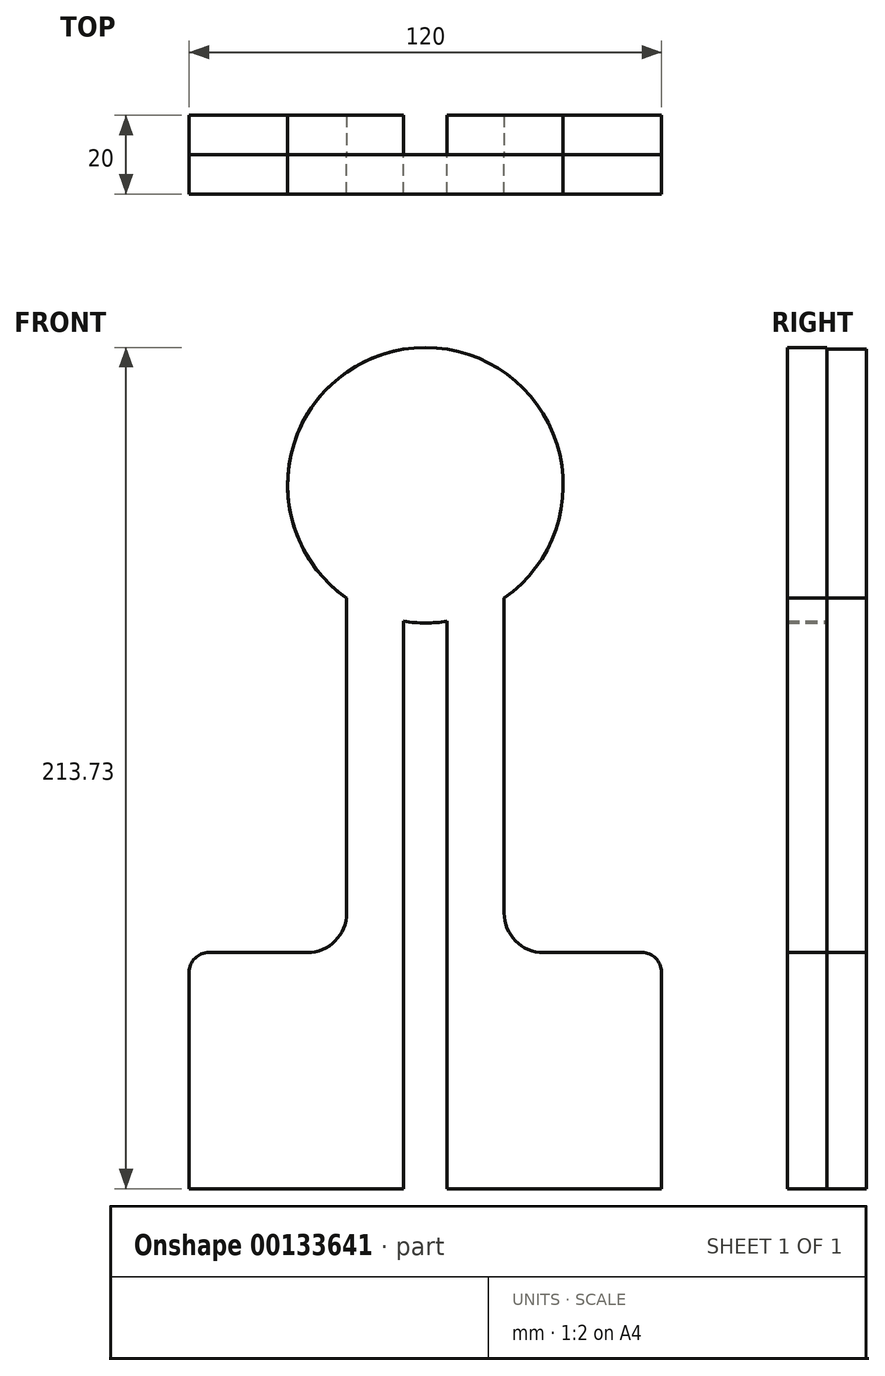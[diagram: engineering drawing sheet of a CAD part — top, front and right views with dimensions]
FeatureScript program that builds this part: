
annotation { "Feature Type Name" : "Feature", "Feature Type Description" : "" }
export const myFeature = defineFeature(function(context is Context, id is Id, definition is map)
    precondition{}
    {
        {
            var Q0;
            Q0=qCreatedBy(makeId("Front.planeOp"),FACE);
            var sketch = newSketch(context, id + "F0", { "sketchPlane" : qUnion([Q0])});
            skCircle(sketch, "E0", {"center": v(0, 111.6) * mm, "radius": 35 * mm});
            skLineSegment(sketch, "E1.bottom", {"start": v(-20, 82.88) * mm, "end": v(20, 82.88) * mm});
            skLineSegment(sketch, "E1.top", {"start": v(-20, -7.12) * mm, "end": v(20, -7.12) * mm});
            skLineSegment(sketch, "E1.left", {"start": v(-20, 82.88) * mm, "end": v(-20, 2.88) * mm});
            skLineSegment(sketch, "E1.right", {"start": v(20, 82.88) * mm, "end": v(20, 2.88) * mm});
            skPoint(sketch, "E1.middle", {"position": v(0, 37.88) * mm});
            skLineSegment(sketch, "E2.bottom", {"start": v(30, -7.12) * mm, "end": v(55, -7.12) * mm});
            skLineSegment(sketch, "E2.top", {"start": v(-60, -67.12) * mm, "end": v(60, -67.12) * mm});
            skLineSegment(sketch, "E2.left", {"start": v(-60, -12.12) * mm, "end": v(-60, -67.12) * mm});
            skLineSegment(sketch, "E2.right", {"start": v(60, -12.12) * mm, "end": v(60, -67.12) * mm});
            skPoint(sketch, "E2.middle", {"position": v(0, -37.12) * mm});
            skLineSegment(sketch, "E3.bottom", {"start": v(5.5, -67.12) * mm, "end": v(-5.5, -67.12) * mm});
            skLineSegment(sketch, "E3.top", {"start": v(5.5, 42.88) * mm, "end": v(-5.5, 42.88) * mm});
            skLineSegment(sketch, "E3.left", {"start": v(5.5, -67.12) * mm, "end": v(5.5, 42.88) * mm});
            skLineSegment(sketch, "E3.right", {"start": v(-5.5, -67.12) * mm, "end": v(-5.5, 42.88) * mm});
            skPoint(sketch, "E3.middle", {"position": v(0, -12.12) * mm});
            skLineSegment(sketch, "E4.bottom", {"start": v(-5.5, 146.17) * mm, "end": v(5.5, 146.17) * mm});
            skLineSegment(sketch, "E4.top", {"start": v(-5.5, 42.88) * mm, "end": v(5.5, 42.88) * mm});
            skLineSegment(sketch, "E4.left", {"start": v(-5.5, 146.17) * mm, "end": v(-5.5, 42.88) * mm});
            skLineSegment(sketch, "E4.right", {"start": v(5.5, 146.17) * mm, "end": v(5.5, 42.88) * mm});
            skPoint(sketch, "E4.middle", {"position": v(0, 94.53) * mm});
            skPoint(sketch, "E5.visualSharp", {"position": v(-60, -7.12) * mm});
            skArc(sketch, "E5.filletArc", {"start": v(-55, -7.12) * mm, "mid": v(-58.54, -8.58) * mm, "end": v(-60, -12.12) * mm});
            skPoint(sketch, "E6.visualSharp", {"position": v(60, -7.12) * mm});
            skArc(sketch, "E6.filletArc", {"start": v(60, -12.12) * mm, "mid": v(58.54, -8.58) * mm, "end": v(55, -7.12) * mm});
            skArc(sketch, "E7.filletArc", {"start": v(20, 2.88) * mm, "mid": v(22.93, -4.19) * mm, "end": v(30, -7.12) * mm});
            skLineSegment(sketch, "E8", {"start": v(-55, -7.12) * mm, "end": v(-30, -7.12) * mm});
            skPoint(sketch, "E9.visualSharp", {"position": v(-20, -7.12) * mm});
            skArc(sketch, "E9.filletArc", {"start": v(-30, -7.12) * mm, "mid": v(-22.93, -4.19) * mm, "end": v(-20, 2.88) * mm});
            skSolve(sketch);
        }
        {
            var Q0;
            {var subQ0=sQuery(id+"F0.wireOp",EDGE,"E1.bottom");var subQ3=sQuery(id+"F0.wireOp",EDGE,"E4.left");var subQ5=makeQuery(id+"F0.imprint","INTERSECT",VERTEX,{"derivedFrom":[subQ0,subQ3]});Q0=makeQuery(id+"F0.imprint","IMPRINT",FACE,{"disambiguationData":[TD([[makeQuery(id+"F0.imprint","IMPRINT",EDGE,{"disambiguationData":[TD([[subQ5,1.0]])],"derivedFrom":subQ0}),1.0]])]});}
            var Q1;
            {var subQ5=sQuery(id+"F0.wireOp",EDGE,"E4.bottom");Q1=makeQuery(id+"F0.imprint","IMPRINT",FACE,{"disambiguationData":[TD([[makeQuery(id+"F0.imprint","IMPRINT",EDGE,{"derivedFrom":subQ5}),-1.0]])]});}
            var Q2;
            {var subQ0=sQuery(id+"F0.wireOp",EDGE,"E1.bottom");var subQ3=sQuery(id+"F0.wireOp",EDGE,"E4.right");var subQ5=makeQuery(id+"F0.imprint","INTERSECT",VERTEX,{"derivedFrom":[subQ0,subQ3]});Q2=makeQuery(id+"F0.imprint","IMPRINT",FACE,{"disambiguationData":[TD([[makeQuery(id+"F0.imprint","IMPRINT",EDGE,{"disambiguationData":[TD([[subQ5,-1.0]])],"derivedFrom":subQ0}),1.0]])]});}
            var Q3;
            {var subQ1=sQuery(id+"F0.wireOp",EDGE,"E0");var subQ3=sQuery(id+"F0.wireOp",EDGE,"E4.right");var subQ4=makeQuery(id+"F0.imprint","INTERSECT",VERTEX,{"derivedFrom":[subQ1,subQ3]});Q3=makeQuery(id+"F0.imprint","IMPRINT",FACE,{"disambiguationData":[TD([[makeQuery(id+"F0.imprint","IMPRINT",EDGE,{"disambiguationData":[TD([[subQ4,1.0]])],"derivedFrom":subQ3}),1.0]])]});}
            var Q4;
            {var subQ0=sQuery(id+"F0.wireOp",EDGE,"E4.left");var subQ1=sQuery(id+"F0.wireOp",EDGE,"E0");var subQ2=makeQuery(id+"F0.imprint","INTERSECT",VERTEX,{"derivedFrom":[subQ1,subQ0]});Q4=makeQuery(id+"F0.imprint","IMPRINT",FACE,{"disambiguationData":[TD([[makeQuery(id+"F0.imprint","IMPRINT",EDGE,{"disambiguationData":[TD([[subQ2,-1.0]])],"derivedFrom":subQ1}),1.0]])]});}
            var Q5;
            {var subQ1=sQuery(id+"F0.wireOp",EDGE,"E0");var subQ3=sQuery(id+"F0.wireOp",EDGE,"E4.left");var subQ4=makeQuery(id+"F0.imprint","INTERSECT",VERTEX,{"derivedFrom":[subQ1,subQ3]});Q5=makeQuery(id+"F0.imprint","IMPRINT",FACE,{"disambiguationData":[TD([[makeQuery(id+"F0.imprint","IMPRINT",EDGE,{"disambiguationData":[TD([[subQ4,1.0]])],"derivedFrom":subQ3}),-1.0]])]});}
            var Q6;
            {var subQ8=sQuery(id+"F0.wireOp",EDGE,"E1.left");Q6=makeQuery(id+"F0.imprint","IMPRINT",FACE,{"disambiguationData":[TD([[makeQuery(id+"F0.imprint","IMPRINT",EDGE,{"derivedFrom":subQ8}),1.0]])]});}
            var Q7;
            {var subQ5=sQuery(id+"F0.wireOp",EDGE,"E1.right");Q7=makeQuery(id+"F0.imprint","IMPRINT",FACE,{"disambiguationData":[TD([[makeQuery(id+"F0.imprint","IMPRINT",EDGE,{"derivedFrom":subQ5}),-1.0]])]});}
            var Q8;
            {var subQ5=sQuery(id+"F0.wireOp",EDGE,"E4.top");Q8=makeQuery(id+"F0.imprint","IMPRINT",FACE,{"disambiguationData":[TD([[makeQuery(id+"F0.imprint","IMPRINT",EDGE,{"derivedFrom":subQ5}),1.0]])]});}
            var Q9;
            {var subQ0=sQuery(id+"F0.wireOp",EDGE,"E4.bottom");Q9=makeQuery(id+"F0.imprint","IMPRINT",FACE,{"disambiguationData":[TD([[makeQuery(id+"F0.imprint","IMPRINT",EDGE,{"derivedFrom":subQ0}),1.0]])]});}
            extrude(context, id + "F1", {"entities" : qUnion([Q0, Q1, Q2, Q3, Q4, Q5, Q6, Q7, Q8, Q9]), "depth" : 10 * mm});
        }
        {
            var Q0;
            {var subQ0=sQuery(id+"F0.wireOp",EDGE,"E1.bottom");var subQ3=sQuery(id+"F0.wireOp",EDGE,"E4.left");var subQ5=makeQuery(id+"F0.imprint","INTERSECT",VERTEX,{"derivedFrom":[subQ0,subQ3]});Q0=makeQuery(id+"F0.imprint","IMPRINT",FACE,{"disambiguationData":[TD([[makeQuery(id+"F0.imprint","IMPRINT",EDGE,{"disambiguationData":[TD([[subQ5,1.0]])],"derivedFrom":subQ0}),1.0]])]});}
            var Q1;
            {var subQ0=sQuery(id+"F0.wireOp",EDGE,"E1.bottom");var subQ3=sQuery(id+"F0.wireOp",EDGE,"E4.right");var subQ5=makeQuery(id+"F0.imprint","INTERSECT",VERTEX,{"derivedFrom":[subQ0,subQ3]});Q1=makeQuery(id+"F0.imprint","IMPRINT",FACE,{"disambiguationData":[TD([[makeQuery(id+"F0.imprint","IMPRINT",EDGE,{"disambiguationData":[TD([[subQ5,-1.0]])],"derivedFrom":subQ0}),1.0]])]});}
            var Q2;
            {var subQ1=sQuery(id+"F0.wireOp",EDGE,"E0");var subQ3=sQuery(id+"F0.wireOp",EDGE,"E4.left");var subQ4=makeQuery(id+"F0.imprint","INTERSECT",VERTEX,{"derivedFrom":[subQ1,subQ3]});Q2=makeQuery(id+"F0.imprint","IMPRINT",FACE,{"disambiguationData":[TD([[makeQuery(id+"F0.imprint","IMPRINT",EDGE,{"disambiguationData":[TD([[subQ4,1.0]])],"derivedFrom":subQ3}),-1.0]])]});}
            var Q3;
            {var subQ1=sQuery(id+"F0.wireOp",EDGE,"E0");var subQ3=sQuery(id+"F0.wireOp",EDGE,"E4.right");var subQ4=makeQuery(id+"F0.imprint","INTERSECT",VERTEX,{"derivedFrom":[subQ1,subQ3]});Q3=makeQuery(id+"F0.imprint","IMPRINT",FACE,{"disambiguationData":[TD([[makeQuery(id+"F0.imprint","IMPRINT",EDGE,{"disambiguationData":[TD([[subQ4,1.0]])],"derivedFrom":subQ3}),1.0]])]});}
            var Q4;
            {var subQ5=sQuery(id+"F0.wireOp",EDGE,"E3.bottom");Q4=makeQuery(id+"F0.imprint","IMPRINT",FACE,{"disambiguationData":[TD([[makeQuery(id+"F0.imprint","IMPRINT",EDGE,{"derivedFrom":subQ5}),-1.0]])]});}
            var Q5;
            {var subQ8=sQuery(id+"F0.wireOp",EDGE,"E1.left");Q5=makeQuery(id+"F0.imprint","IMPRINT",FACE,{"disambiguationData":[TD([[makeQuery(id+"F0.imprint","IMPRINT",EDGE,{"derivedFrom":subQ8}),1.0]])]});}
            var Q6;
            {var subQ5=sQuery(id+"F0.wireOp",EDGE,"E1.right");Q6=makeQuery(id+"F0.imprint","IMPRINT",FACE,{"disambiguationData":[TD([[makeQuery(id+"F0.imprint","IMPRINT",EDGE,{"derivedFrom":subQ5}),-1.0]])]});}
            var Q7;
            {var subQ5=sQuery(id+"F0.wireOp",EDGE,"E4.top");Q7=makeQuery(id+"F0.imprint","IMPRINT",FACE,{"disambiguationData":[TD([[makeQuery(id+"F0.imprint","IMPRINT",EDGE,{"derivedFrom":subQ5}),-1.0]])]});}
            extrude(context, id + "F2", {"entities" : qUnion([Q0, Q1, Q2, Q3, Q4, Q5, Q6, Q7]), "oppositeDirection" : true, "depth" : 10 * mm});
        }
    });
